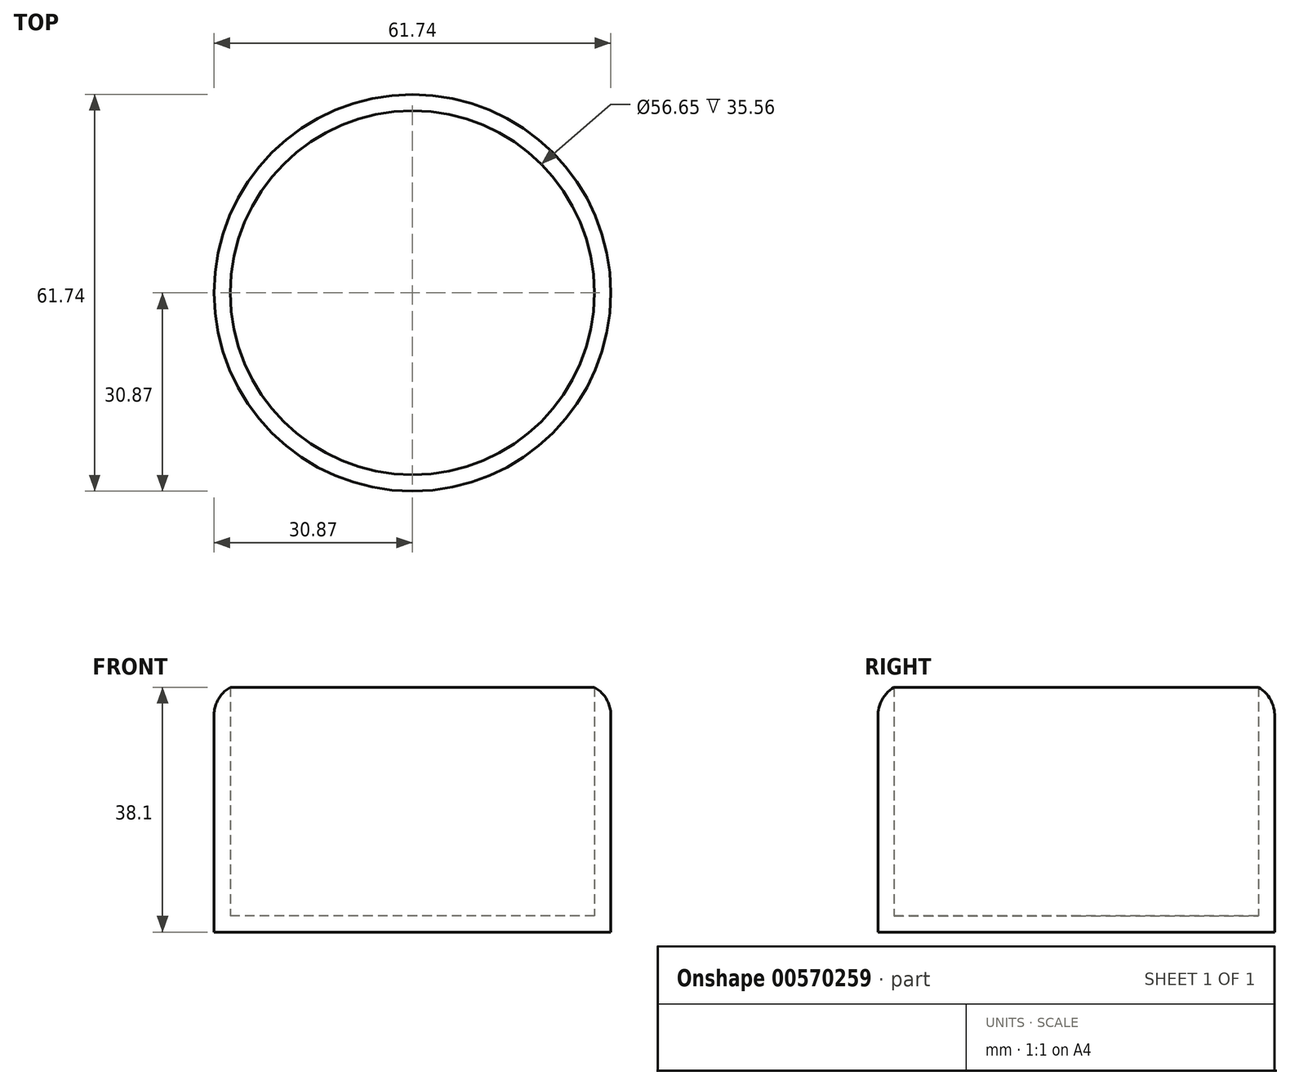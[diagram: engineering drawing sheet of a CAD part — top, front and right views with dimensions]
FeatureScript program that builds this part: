
annotation { "Feature Type Name" : "Feature", "Feature Type Description" : "" }
export const myFeature = defineFeature(function(context is Context, id is Id, definition is map)
    precondition{}
    {
        {
            var Q0;
            Q0=qCreatedBy(makeId("Top.planeOp"),FACE);
            var sketch = newSketch(context, id + "F0", { "sketchPlane" : qUnion([Q0])});
            skCircle(sketch, "E0", {"center": v(0, 0) * mm, "radius": 30.87 * mm});
            skSolve(sketch);
        }
        {
            var Q0;
            Q0 = qSketchRegion(id + "F0", true);
            extrude(context, id + "F1", {"entities" : qUnion([Q0]), "endBound" : BoundingType.SYMMETRIC, "depth" : 38.1 * mm, "offsetDistance" : 25.4 * mm});
        }
        {
            var Q0;
            Q0=makeQuery(id+"F1.opExtrude","CAP_FACE",FACE,{"disambiguationData":[OSD([sQuery(id+"F0.wireOp",EDGE,"E0")])],"isStart":false});
            shell(context, id + "F2", {"entities" : qUnion([Q0]), "thickness" : 2.54 * mm});
        }
        {
            var Q0;
            Q0=makeQuery(id+"F1.opExtrude","CAP_EDGE",EDGE,{"disambiguationData":[OSD([sQuery(id+"F0.wireOp",EDGE,"E0")])],"isStart":false});
            fillet(context, id + "F3", {"entities" : qUnion([Q0]), "radius" : 5.08 * mm, "tangentPropagation" : true, "allowEdgeOverflow" : false});
        }
    });
